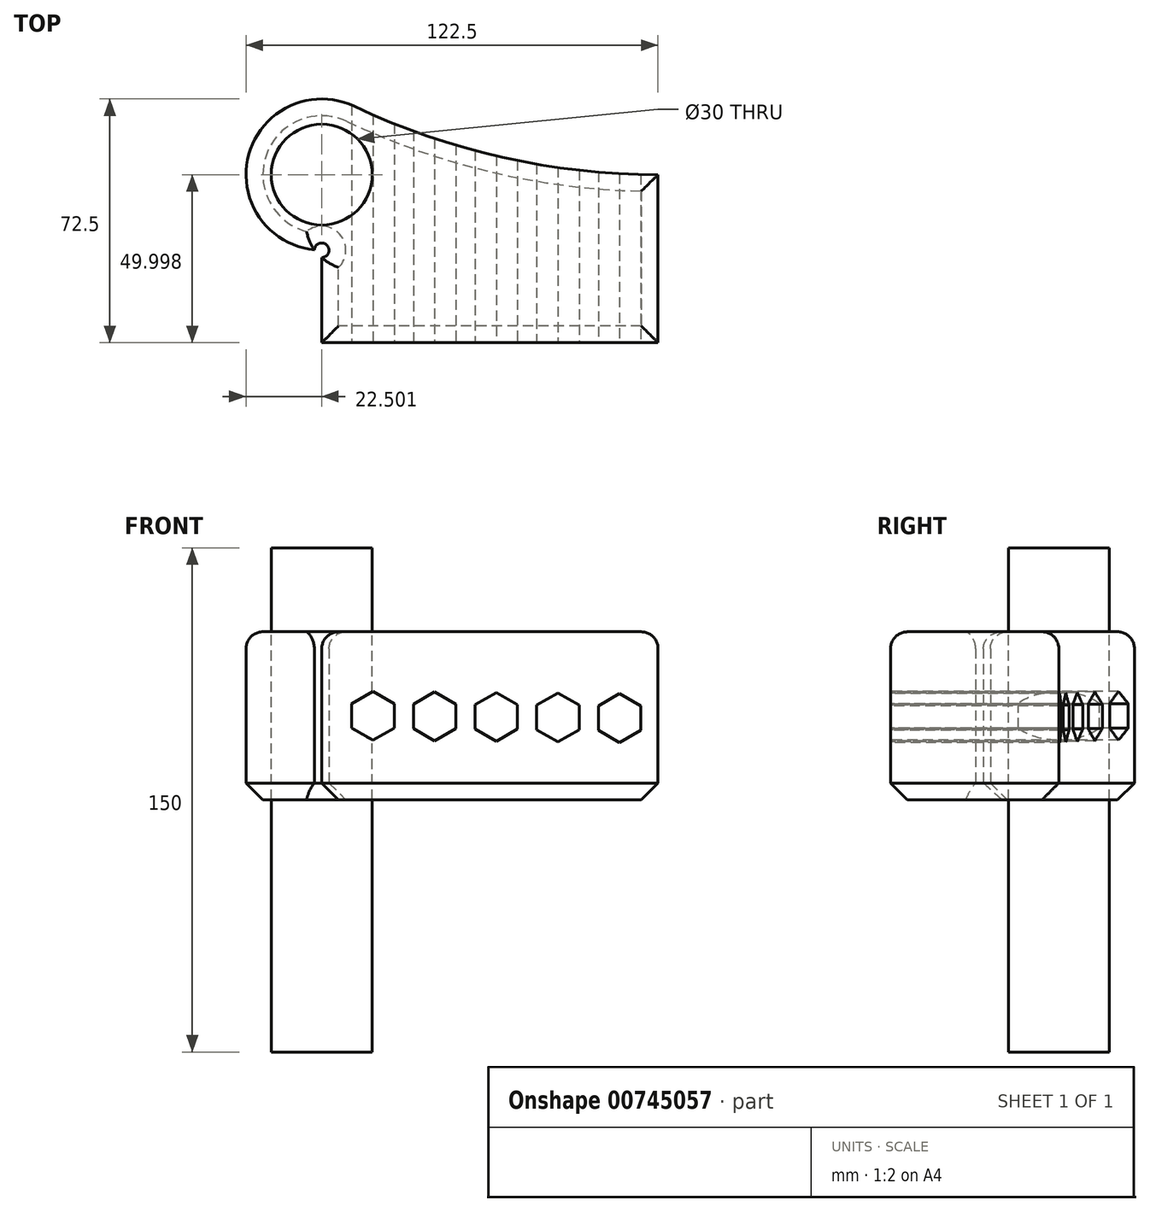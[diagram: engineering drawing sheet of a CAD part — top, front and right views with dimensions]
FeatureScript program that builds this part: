
annotation { "Feature Type Name" : "Feature", "Feature Type Description" : "" }
export const myFeature = defineFeature(function(context is Context, id is Id, definition is map)
    precondition{}
    {
        {
            var Q0;
            Q0=qCreatedBy(makeId("Top.planeOp"),FACE);
            var sketch = newSketch(context, id + "F0", { "sketchPlane" : qUnion([Q0])});
            skLineSegment(sketch, "E0.bottom", {"start": v(-52.07, 26.03) * mm, "end": v(47.93, 26.03) * mm});
            skLineSegment(sketch, "E0.top", {"start": v(-52.07, -23.97) * mm, "end": v(47.93, -23.97) * mm});
            skLineSegment(sketch, "E0.left", {"start": v(-52.07, 26.03) * mm, "end": v(-52.07, -23.97) * mm});
            skLineSegment(sketch, "E0.right", {"start": v(47.93, 26.03) * mm, "end": v(47.93, -23.97) * mm});
            skCircle(sketch, "E1", {"center": v(-52.07, 26.03) * mm, "radius": 22.5 * mm});
            skArc(sketch, "E2", {"start": v(-42.43, 46.36) * mm, "mid": v(1.62, 31.17) * mm, "end": v(47.93, 26.03) * mm});
            skCircle(sketch, "E3", {"center": v(-52.07, 26.03) * mm, "radius": 15 * mm});
            skCircle(sketch, "E4", {"center": v(-52.07, 3.53) * mm, "radius": 2.18 * mm});
            skSolve(sketch);
        }
        {
            var Q0;
            {var subQ2=sQuery(id+"F0.wireOp",EDGE,"E0.bottom");var subQ4=sQuery(id+"F0.wireOp",EDGE,"E3");var subQ9=makeQuery(id+"F0.imprint","INTERSECT",VERTEX,{"derivedFrom":[subQ2,subQ4]});Q0=makeQuery(id+"F0.imprint","IMPRINT",FACE,{"disambiguationData":[TD([[makeQuery(id+"F0.imprint","IMPRINT",EDGE,{"disambiguationData":[TD([[subQ9,-1.0]])],"derivedFrom":subQ2}),1.0]])]});}
            var Q1;
            {var subQ0=sQuery(id+"F0.wireOp",EDGE,"E3");var subQ1=sQuery(id+"F0.wireOp",EDGE,"E0.bottom");var subQ2=makeQuery(id+"F0.imprint","INTERSECT",VERTEX,{"derivedFrom":[subQ1,subQ0]});Q1=makeQuery(id+"F0.imprint","IMPRINT",FACE,{"disambiguationData":[TD([[makeQuery(id+"F0.imprint","IMPRINT",EDGE,{"disambiguationData":[TD([[subQ2,-1.0]])],"derivedFrom":subQ1}),-1.0]])]});}
            var Q2;
            {var subQ0=sQuery(id+"F0.wireOp",EDGE,"E2");Q2=makeQuery(id+"F0.imprint","IMPRINT",FACE,{"disambiguationData":[TD([[makeQuery(id+"F0.imprint","IMPRINT",EDGE,{"derivedFrom":subQ0}),-1.0]])]});}
            var Q3;
            {var subQ2=sQuery(id+"F0.wireOp",EDGE,"E0.top");Q3=makeQuery(id+"F0.imprint","IMPRINT",FACE,{"disambiguationData":[TD([[makeQuery(id+"F0.imprint","IMPRINT",EDGE,{"derivedFrom":subQ2}),1.0]])]});}
            extrude(context, id + "F1", {"entities" : qUnion([Q0, Q1, Q2, Q3]), "depth" : 50 * mm, "offsetDistance" : 25 * mm});
        }
        {
            var Q0;
            {var subQ0=sQuery(id+"F0.wireOp",EDGE,"E0.left");var subQ1=sQuery(id+"F0.wireOp",EDGE,"E0.bottom");var subQ2=makeQuery(id+"F0.imprint","INTERSECT",VERTEX,{"derivedFrom":[subQ1,subQ0]});Q0=makeQuery(id+"F0.imprint","IMPRINT",FACE,{"disambiguationData":[TD([[makeQuery(id+"F0.imprint","IMPRINT",EDGE,{"disambiguationData":[TD([[subQ2,-1.0]])],"derivedFrom":subQ1}),-1.0]])]});}
            var Q1;
            {var subQ0=sQuery(id+"F0.wireOp",EDGE,"E0.left");var subQ1=sQuery(id+"F0.wireOp",EDGE,"E0.bottom");var subQ2=makeQuery(id+"F0.imprint","INTERSECT",VERTEX,{"derivedFrom":[subQ1,subQ0]});Q1=makeQuery(id+"F0.imprint","IMPRINT",FACE,{"disambiguationData":[TD([[makeQuery(id+"F0.imprint","IMPRINT",EDGE,{"disambiguationData":[TD([[subQ2,-1.0]])],"derivedFrom":subQ1}),1.0]])]});}
            extrude(context, id + "F2", {"entities" : qUnion([Q0, Q1]), "endBound" : BoundingType.SYMMETRIC, "oppositeDirection" : true, "depth" : 150 * mm, "offsetDistance" : 25 * mm});
        }
        {
            var Q0;
            Q0=makeQuery(id+"F1.opExtrude","SWEPT_FACE",FACE,{"disambiguationData":[OSD([sQuery(id+"F0.wireOp",EDGE,"E0.top")])]});
            var sketch = newSketch(context, id + "F3", { "sketchPlane" : qUnion([Q0])});
            skCircle(sketch, "E5.cCircle", {"center": v(-36.83, 25) * mm, "radius": 6.3 * mm, "construction": true});
            skPoint(sketch, "E5.cCircle.centerSnap0", {"position": v(-52.07, 25) * mm});
            skLineSegment(sketch, "E5.0", {"start": v(-30.53, 28.64) * mm, "end": v(-30.53, 21.36) * mm});
            skLineSegment(sketch, "E5.1", {"start": v(-30.53, 21.36) * mm, "end": v(-36.83, 17.73) * mm});
            skLineSegment(sketch, "E5.2", {"start": v(-36.83, 17.73) * mm, "end": v(-43.13, 21.36) * mm});
            skLineSegment(sketch, "E5.3", {"start": v(-43.13, 21.36) * mm, "end": v(-43.13, 28.64) * mm});
            skLineSegment(sketch, "E5.4", {"start": v(-43.13, 28.64) * mm, "end": v(-36.83, 32.27) * mm});
            skLineSegment(sketch, "E5.5", {"start": v(-36.83, 32.27) * mm, "end": v(-30.53, 28.64) * mm});
            skPoint(sketch, "E5.0.midPoint", {"position": v(-30.53, 25) * mm});
            skLineSegment(sketch, "E6.1.0.0", {"start": v(-24.8, 28.47) * mm, "end": v(-18.5, 32.1) * mm});
            skLineSegment(sketch, "E6.1.0.1", {"start": v(-24.8, 21.2) * mm, "end": v(-24.8, 28.47) * mm});
            skCircle(sketch, "E6.1.0.2", {"center": v(-18.5, 24.84) * mm, "radius": 6.3 * mm, "construction": true});
            skLineSegment(sketch, "E6.1.0.3", {"start": v(-18.5, 17.56) * mm, "end": v(-24.8, 21.2) * mm});
            skLineSegment(sketch, "E6.1.0.4", {"start": v(-12.2, 21.2) * mm, "end": v(-18.5, 17.56) * mm});
            skLineSegment(sketch, "E6.1.0.5", {"start": v(-12.2, 28.47) * mm, "end": v(-12.2, 21.2) * mm});
            skLineSegment(sketch, "E6.1.0.6", {"start": v(-18.5, 32.1) * mm, "end": v(-12.2, 28.47) * mm});
            skLineSegment(sketch, "E6.2.0.0", {"start": v(-6.47, 28.3) * mm, "end": v(-0.17, 31.94) * mm});
            skLineSegment(sketch, "E6.2.0.1", {"start": v(-6.47, 21.04) * mm, "end": v(-6.47, 28.3) * mm});
            skCircle(sketch, "E6.2.0.2", {"center": v(-0.17, 24.67) * mm, "radius": 6.3 * mm, "construction": true});
            skLineSegment(sketch, "E6.2.0.3", {"start": v(-0.17, 17.4) * mm, "end": v(-6.47, 21.04) * mm});
            skLineSegment(sketch, "E6.2.0.4", {"start": v(6.12, 21.04) * mm, "end": v(-0.17, 17.4) * mm});
            skLineSegment(sketch, "E6.2.0.5", {"start": v(6.12, 28.3) * mm, "end": v(6.12, 21.04) * mm});
            skLineSegment(sketch, "E6.2.0.6", {"start": v(-0.17, 31.94) * mm, "end": v(6.12, 28.3) * mm});
            skLineSegment(sketch, "E6.3.0.0", {"start": v(11.86, 28.14) * mm, "end": v(18.16, 31.78) * mm});
            skLineSegment(sketch, "E6.3.0.1", {"start": v(11.86, 20.87) * mm, "end": v(11.86, 28.14) * mm});
            skCircle(sketch, "E6.3.0.2", {"center": v(18.16, 24.5) * mm, "radius": 6.3 * mm, "construction": true});
            skLineSegment(sketch, "E6.3.0.3", {"start": v(18.16, 17.24) * mm, "end": v(11.86, 20.87) * mm});
            skLineSegment(sketch, "E6.3.0.4", {"start": v(24.45, 20.87) * mm, "end": v(18.16, 17.24) * mm});
            skLineSegment(sketch, "E6.3.0.5", {"start": v(24.45, 28.14) * mm, "end": v(24.45, 20.87) * mm});
            skLineSegment(sketch, "E6.3.0.6", {"start": v(18.16, 31.78) * mm, "end": v(24.45, 28.14) * mm});
            skLineSegment(sketch, "E6.4.0.0", {"start": v(30.19, 27.98) * mm, "end": v(36.49, 31.62) * mm});
            skLineSegment(sketch, "E6.4.0.1", {"start": v(30.19, 20.7) * mm, "end": v(30.19, 27.98) * mm});
            skCircle(sketch, "E6.4.0.2", {"center": v(36.49, 24.34) * mm, "radius": 6.3 * mm, "construction": true});
            skLineSegment(sketch, "E6.4.0.3", {"start": v(36.49, 17.07) * mm, "end": v(30.19, 20.7) * mm});
            skLineSegment(sketch, "E6.4.0.4", {"start": v(42.78, 20.7) * mm, "end": v(36.49, 17.07) * mm});
            skLineSegment(sketch, "E6.4.0.5", {"start": v(42.78, 27.98) * mm, "end": v(42.78, 20.7) * mm});
            skLineSegment(sketch, "E6.4.0.6", {"start": v(36.49, 31.62) * mm, "end": v(42.78, 27.98) * mm});
            skLineSegment(sketch, "E6.direction1", {"start": v(-43.13, 21.36) * mm, "end": v(-24.8, 21.2) * mm, "construction": true});
            skSolve(sketch);
        }
        {
            var Q0;
            Q0 = qSketchRegion(id + "F3", true);
            extrude(context, id + "F4", {"entities" : qUnion([Q0]), "operationType" : NewBodyOperationType.REMOVE, "endBound" : BoundingType.THROUGH_ALL, "oppositeDirection" : true, "depth" : 25 * mm, "offsetDistance" : 25 * mm});
        }
        {
            var Q0;
            Q0=makeQuery(id+"F1.opExtrude","CAP_EDGE",EDGE,{"disambiguationData":[OSD([sQuery(id+"F0.wireOp",EDGE,"E0.top")])],"isStart":false});
            var Q1;
            Q1=makeQuery(id+"F1.opExtrude","CAP_EDGE",EDGE,{"disambiguationData":[OSD([sQuery(id+"F0.wireOp",EDGE,"E0.right")])],"isStart":false});
            var Q2;
            Q2=makeQuery(id+"F1.opExtrude","CAP_EDGE",EDGE,{"disambiguationData":[OSD([sQuery(id+"F0.wireOp",EDGE,"E2")])],"isStart":false});
            var Q3;
            Q3=makeQuery(id+"F1.opExtrude","CAP_EDGE",EDGE,{"disambiguationData":[OSD([sQuery(id+"F0.wireOp",EDGE,"E1")])],"isStart":false});
            var Q4;
            Q4=makeQuery(id+"F1.opExtrude","CAP_EDGE",EDGE,{"disambiguationData":[OSD([sQuery(id+"F0.wireOp",EDGE,"E0.left")])],"isStart":false});
            var Q5;
            Q5=makeQuery(id+"F1.opExtrude","CAP_EDGE",EDGE,{"disambiguationData":[OSD([sQuery(id+"F0.wireOp",EDGE,"E4")])],"isStart":false});
            fillet(context, id + "F5", {"entities" : qUnion([Q0, Q1, Q2, Q3, Q4, Q5]), "radius" : 5 * mm, "tangentPropagation" : true, "allowEdgeOverflow" : false});
        }
        {
            var Q0;
            Q0=makeQuery(id+"F1.opExtrude","CAP_EDGE",EDGE,{"disambiguationData":[OSD([sQuery(id+"F0.wireOp",EDGE,"E0.top")])],"isStart":true});
            var Q1;
            Q1=makeQuery(id+"F1.opExtrude","CAP_EDGE",EDGE,{"disambiguationData":[OSD([sQuery(id+"F0.wireOp",EDGE,"E0.right")])],"isStart":true});
            var Q2;
            Q2=makeQuery(id+"F1.opExtrude","CAP_EDGE",EDGE,{"disambiguationData":[OSD([sQuery(id+"F0.wireOp",EDGE,"E2")])],"isStart":true});
            var Q3;
            Q3=makeQuery(id+"F1.opExtrude","CAP_EDGE",EDGE,{"disambiguationData":[OSD([sQuery(id+"F0.wireOp",EDGE,"E1")])],"isStart":true});
            var Q4;
            Q4=makeQuery(id+"F1.opExtrude","CAP_EDGE",EDGE,{"disambiguationData":[OSD([sQuery(id+"F0.wireOp",EDGE,"E4")])],"isStart":true});
            var Q5;
            Q5=makeQuery(id+"F1.opExtrude","CAP_EDGE",EDGE,{"disambiguationData":[OSD([sQuery(id+"F0.wireOp",EDGE,"E0.left")])],"isStart":true});
            chamfer(context, id + "F6", {"entities" : qUnion([Q0, Q1, Q2, Q3, Q4, Q5]), "width" : 5 * mm, "tangentPropagation" : true});
        }
    });
